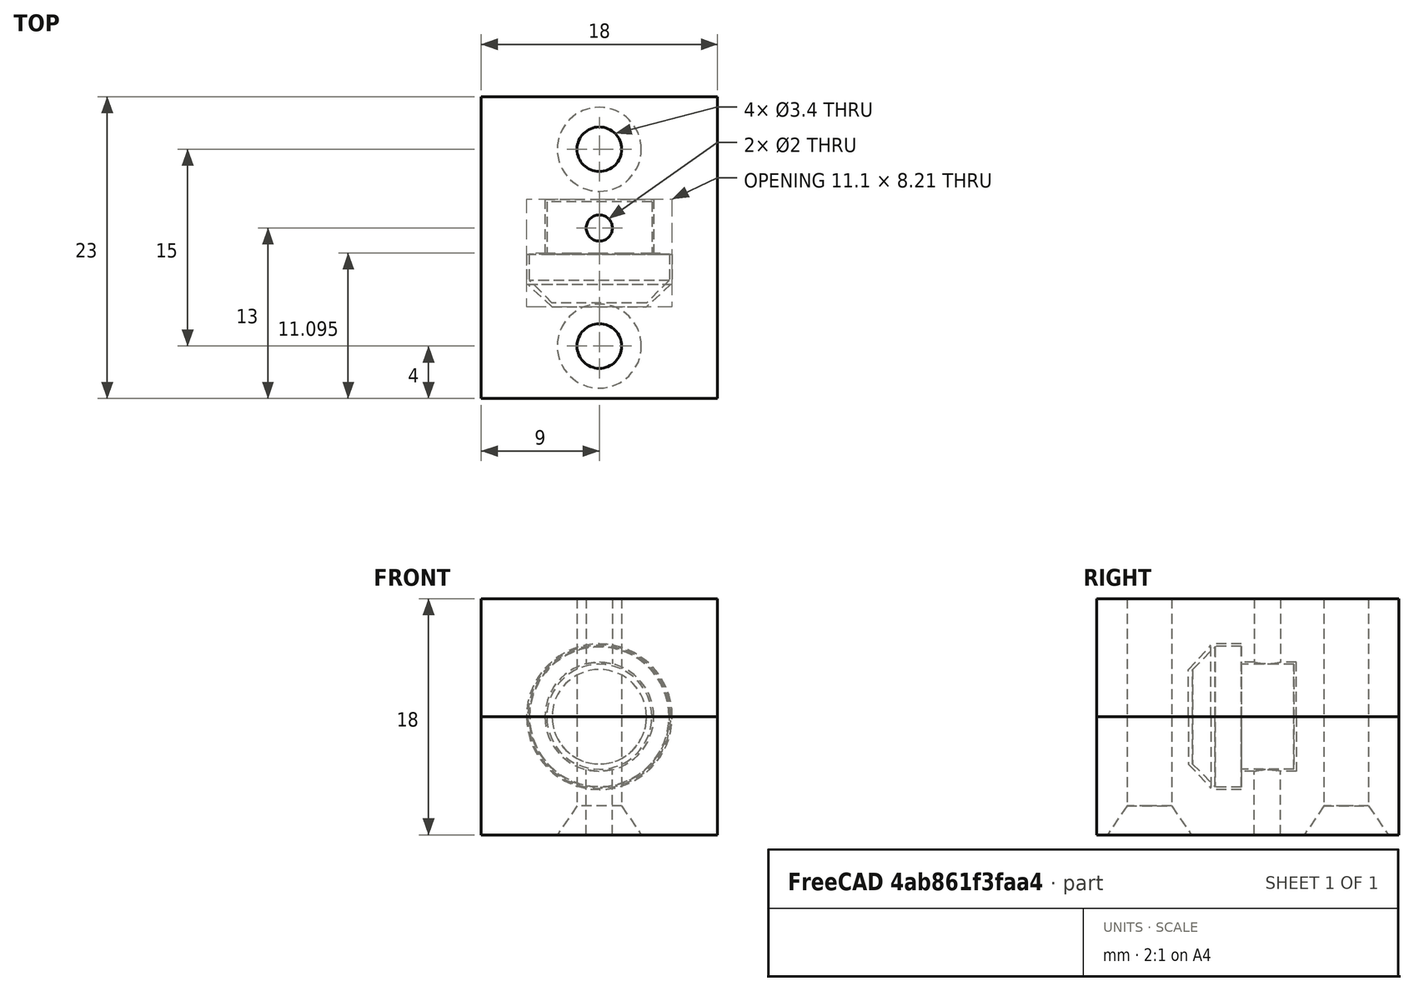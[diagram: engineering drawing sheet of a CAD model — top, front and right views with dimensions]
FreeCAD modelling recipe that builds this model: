
FCSTD DOCUMENT  (FreeCAD 0.18R16146 (Git))
Label: Nylon Bevel Gear Jig
License: All rights reserved
LicenseURL: http://en.wikipedia.org/wiki/All_rights_reserved
objects: Part::Cylinder×12, Part::Cut×6, Part::Cone×5, Part::MultiFuse×5, Part::Box×2, Part::Fuse×2
note: 32 computed .brp shape members not serialized (recipe doc carries the construction recipe); baked Part::Feature solids carry a one-line shape summary decoded from their .brp

FEATURE [Part::Cylinder] Cylinder081017  label="Cylinder081014"
  Angle = 360
  AttacherType = Attacher::AttachEngine3D
  Height = 4.2
  Placement = pos=(0,2.2,9) rot=(1,0,0;1.5708rad)
  Radius = 4.15
FEATURE [Part::Cylinder] Cylinder081018  label="Cylinder081015"
  Angle = 360
  AttacherType = Attacher::AttachEngine3D
  Height = 2.3
  Placement = pos=(0,-2,9) rot=(1,0,0;1.5708rad)
  Radius = 5.55
FEATURE [Part::Cone] Cone004
  Angle = 360
  AttacherType = Attacher::AttachEngine3D
  Height = 1.71
  Placement = pos=(0,-4.3,9) rot=(1,0,0;1.5708rad)
  Radius1 = 5.45
  Radius2 = 3.6
FEATURE [Part::Box] Box  label="Cube"
  AttacherType = Attacher::AttachEngine3D
  Height = 9
  Length = 18
  Placement = pos=(-9,-13,0) rot=(0,0,1;0rad)
  Width = 23
FEATURE [Part::Cylinder] Cylinder
  Angle = 360
  AttacherType = Attacher::AttachEngine3D
  Height = 28
  Radius = 1
FEATURE [Part::Cylinder] Cylinder081020
  Angle = 360
  AttacherType = Attacher::AttachEngine3D
  Height = 10
  Radius = 1.7
FEATURE [Part::Cone] Cone
  Angle = 360
  AttacherType = Attacher::AttachEngine3D
  Height = 2.2
  Placement = pos=(0,0,8.8) rot=(0,0,1;0rad)
  Radius1 = 1.7
  Radius2 = 3.2
FEATURE [Part::Fuse] Fusion
  Base = -> Cylinder081020
  Placement = pos=(0,6,11) rot=(1,0,0;3.14159rad)
  Tool = -> Cone
FEATURE [Part::Cone] Cone005
  Angle = 360
  AttacherType = Attacher::AttachEngine3D
  Height = 2.2
  Placement = pos=(0,0,8.8) rot=(0,0,1;0rad)
  Radius1 = 1.7
  Radius2 = 3.2
FEATURE [Part::Cylinder] Cylinder081021
  Angle = 360
  AttacherType = Attacher::AttachEngine3D
  Height = 10
  Radius = 1.7
FEATURE [Part::Fuse] Fusion103077013004017008011031
  Base = -> Cylinder081021
  Placement = pos=(0,-9,11) rot=(1,0,0;3.14159rad)
  Tool = -> Cone005
FEATURE [Part::MultiFuse] Fusion103077013004017008011032
  Shapes = -> [Fusion103077013004017008011031,Fusion]
FEATURE [Part::Cut] Cut
  Base = -> Box
  Tool = -> Cylinder
FEATURE [Part::Cut] Cut001
  Base = -> Cut
  Tool = -> Fusion103077013004017008011032
FEATURE [Part::Cone] Cone006
  Angle = 360
  AttacherType = Attacher::AttachEngine3D
  Height = 1.71
  Placement = pos=(0,-4,9) rot=(1,0,0;1.5708rad)
  Radius1 = 5.31
  Radius2 = 3.6
FEATURE [Part::Cylinder] Cylinder081022
  Angle = 360
  AttacherType = Attacher::AttachEngine3D
  Height = 2
  Placement = pos=(0,-2,9) rot=(1,0,0;1.5708rad)
  Radius = 5.355
FEATURE [Part::Cylinder] Cylinder081023
  Angle = 360
  AttacherType = Attacher::AttachEngine3D
  Height = 4
  Placement = pos=(0,2,9) rot=(1,0,0;1.5708rad)
  Radius = 4
FEATURE [Part::MultiFuse] Fusion103077013004017008011033  label="Gear"
  Shapes = -> [Cone006,Cylinder081022,Cylinder081023]
FEATURE [Part::MultiFuse] Fusion103077013004017008011034  label="Gear Hole"
  Shapes = -> [Cylinder081017,Cylinder081018,Cone004]
FEATURE [Part::Cut] Cut002  label="Countersunk Block"
  Base = -> Cut001
  Tool = -> Fusion103077013004017008011034
FEATURE [Part::Box] Box001  label="Cube001"
  AttacherType = Attacher::AttachEngine3D
  Height = 9
  Length = 18
  Placement = pos=(-9,-13,0) rot=(0,0,1;0rad)
  Width = 23
FEATURE [Part::Cylinder] Cylinder081024
  Angle = 360
  AttacherType = Attacher::AttachEngine3D
  Height = 4.2
  Placement = pos=(0,2.2,9) rot=(1,0,0;1.5708rad)
  Radius = 4.15
FEATURE [Part::Cylinder] Cylinder081025
  Angle = 360
  AttacherType = Attacher::AttachEngine3D
  Height = 11
  Placement = pos=(0,6,-1) rot=(0,0,1;0rad)
  Radius = 1.7
FEATURE [Part::Cylinder] Cylinder081026
  Angle = 360
  AttacherType = Attacher::AttachEngine3D
  Height = 28
  Radius = 1
FEATURE [Part::Cut] Cut004
  Base = -> Box001
  Tool = -> Cylinder081026
FEATURE [Part::Cone] Cone008
  Angle = 360
  AttacherType = Attacher::AttachEngine3D
  Height = 1.71
  Placement = pos=(0,-4.3,9) rot=(1,0,0;1.5708rad)
  Radius1 = 5.45
  Radius2 = 3.6
FEATURE [Part::Cylinder] Cylinder081027
  Angle = 360
  AttacherType = Attacher::AttachEngine3D
  Height = 2.3
  Placement = pos=(0,-2,9) rot=(1,0,0;1.5708rad)
  Radius = 5.55
FEATURE [Part::MultiFuse] Fusion103077013004017008011038  label="Gear Hole001"
  Shapes = -> [Cylinder081024,Cylinder081027,Cone008]
FEATURE [Part::Cylinder] Cylinder081028
  Angle = 360
  AttacherType = Attacher::AttachEngine3D
  Height = 11
  Placement = pos=(0,-9,-1) rot=(0,0,1;0rad)
  Radius = 1.7
FEATURE [Part::MultiFuse] Fusion103077013004017008011039
  Shapes = -> [Cylinder081028,Cylinder081025]
FEATURE [Part::Cut] Cut005
  Base = -> Cut004
  Tool = -> Fusion103077013004017008011039
FEATURE [Part::Cut] Cut006  label="Straight ScrewHole Block"
  Base = -> Cut005
  Placement = pos=(4e-16,9e-16,18) rot=(0,1,0;3.14159rad)
  Tool = -> Fusion103077013004017008011038
